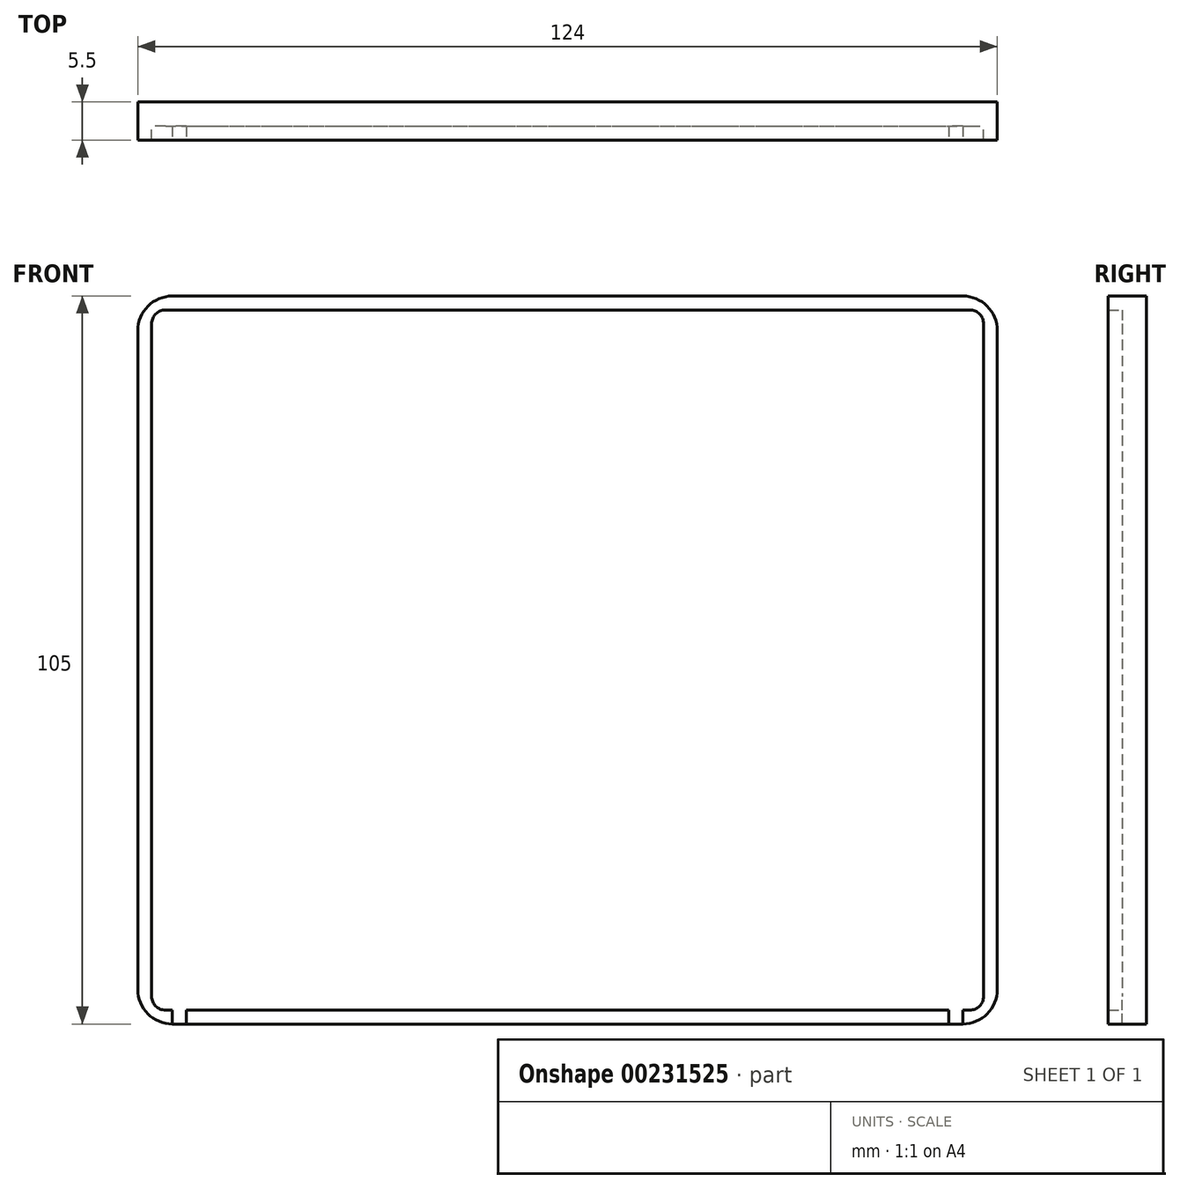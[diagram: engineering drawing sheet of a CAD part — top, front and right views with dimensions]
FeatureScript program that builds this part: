
annotation { "Feature Type Name" : "Feature", "Feature Type Description" : "" }
export const myFeature = defineFeature(function(context is Context, id is Id, definition is map)
    precondition{}
    {
        {
            var Q0;
            Q0=qCreatedBy(makeId("Front.planeOp"),FACE);
            var sketch = newSketch(context, id + "F0", { "sketchPlane" : qUnion([Q0])});
            skLineSegment(sketch, "E0.bottom", {"start": v(62, -52.5) * mm, "end": v(-62, -52.5) * mm});
            skLineSegment(sketch, "E0.top", {"start": v(62, 52.5) * mm, "end": v(-62, 52.5) * mm});
            skLineSegment(sketch, "E0.left", {"start": v(62, -52.5) * mm, "end": v(62, 52.5) * mm});
            skLineSegment(sketch, "E0.right", {"start": v(-62, -52.5) * mm, "end": v(-62, 52.5) * mm});
            skPoint(sketch, "E0.middle", {"position": v(0, 0) * mm});
            skLineSegment(sketch, "E1.bottom", {"start": v(-60, 50.5) * mm, "end": v(60, 50.5) * mm});
            skLineSegment(sketch, "E1.top", {"start": v(-60, -50.5) * mm, "end": v(60, -50.5) * mm});
            skLineSegment(sketch, "E1.left", {"start": v(-60, 50.5) * mm, "end": v(-60, -50.5) * mm});
            skLineSegment(sketch, "E1.right", {"start": v(60, 50.5) * mm, "end": v(60, -50.5) * mm});
            skSolve(sketch);
        }
        {
            var Q0;
            Q0=makeQuery(id+"F0.imprint","IMPRINT",FACE,{"disambiguationData":[TD([[makeQuery(id+"F0.imprint","IMPRINT",EDGE,{"derivedFrom":sQuery(id+"F0.wireOp",EDGE,"E1.bottom")}),-1.0]])]});
            extrude(context, id + "F1", {"entities" : qUnion([Q0]), "depth" : 4 * mm});
        }
        {
            var Q0;
            Q0 = qSketchRegion(id + "F0", true);
            extrude(context, id + "F2", {"entities" : qUnion([Q0]), "operationType" : NewBodyOperationType.ADD, "depth" : 5 * mm});
        }
        {
            var Q0;
            Q0=makeQuery(id+"F2.opExtrude","CAP_FACE",FACE,{"disambiguationData":[OSD([sQuery(id+"F0.wireOp",EDGE,"E0.bottom"),sQuery(id+"F0.wireOp",EDGE,"E0.top"),sQuery(id+"F0.wireOp",EDGE,"E0.left"),sQuery(id+"F0.wireOp",EDGE,"E0.right"),sQuery(id+"F0.wireOp",EDGE,"E1.bottom"),sQuery(id+"F0.wireOp",EDGE,"E1.top"),sQuery(id+"F0.wireOp",EDGE,"E1.left"),sQuery(id+"F0.wireOp",EDGE,"E1.right")])],"isStart":false});
            extrude(context, id + "F3", {"entities" : qUnion([Q0]), "operationType" : NewBodyOperationType.ADD, "depth" : .5 * mm, "offsetDistance" : 25 * mm});
        }
        {
            var Q0;
            {var subQ0=sQuery(id+"F0.wireOp",EDGE,"E0.left");var subQ1=sQuery(id+"F0.wireOp",EDGE,"E0.bottom");Q0=makeQuery(id+"F3.boolean.opBoolean","MERGE",EDGE,{"derivedFrom":[makeQuery(id+"F2.opExtrude","SWEPT_EDGE",EDGE,{"disambiguationData":[OSD([subQ1,subQ0])]}),makeQuery(id+"F3.opExtrude","SWEPT_EDGE",EDGE,{"disambiguationData":[OSD([subQ1,subQ0])]})]});}
            var Q1;
            {var subQ0=sQuery(id+"F0.wireOp",EDGE,"E0.right");var subQ1=sQuery(id+"F0.wireOp",EDGE,"E0.bottom");Q1=makeQuery(id+"F3.boolean.opBoolean","MERGE",EDGE,{"derivedFrom":[makeQuery(id+"F2.opExtrude","SWEPT_EDGE",EDGE,{"disambiguationData":[OSD([subQ1,subQ0])]}),makeQuery(id+"F3.opExtrude","SWEPT_EDGE",EDGE,{"disambiguationData":[OSD([subQ1,subQ0])]})]});}
            var Q2;
            {var subQ0=sQuery(id+"F0.wireOp",EDGE,"E0.right");var subQ1=sQuery(id+"F0.wireOp",EDGE,"E0.top");Q2=makeQuery(id+"F3.boolean.opBoolean","MERGE",EDGE,{"derivedFrom":[makeQuery(id+"F2.opExtrude","SWEPT_EDGE",EDGE,{"disambiguationData":[OSD([subQ1,subQ0])]}),makeQuery(id+"F3.opExtrude","SWEPT_EDGE",EDGE,{"disambiguationData":[OSD([subQ1,subQ0])]})]});}
            var Q3;
            {var subQ0=sQuery(id+"F0.wireOp",EDGE,"E0.left");var subQ1=sQuery(id+"F0.wireOp",EDGE,"E0.top");Q3=makeQuery(id+"F3.boolean.opBoolean","MERGE",EDGE,{"derivedFrom":[makeQuery(id+"F2.opExtrude","SWEPT_EDGE",EDGE,{"disambiguationData":[OSD([subQ1,subQ0])]}),makeQuery(id+"F3.opExtrude","SWEPT_EDGE",EDGE,{"disambiguationData":[OSD([subQ1,subQ0])]})]});}
            fillet(context, id + "F4", {"entities" : qUnion([Q0, Q1, Q2, Q3]), "radius" : 5 * mm, "tangentPropagation" : true, "allowEdgeOverflow" : false});
        }
        {
            var Q0;
            {var subQ0=sQuery(id+"F0.wireOp",EDGE,"E1.right");var subQ1=sQuery(id+"F0.wireOp",EDGE,"E1.bottom");Q0=makeQuery(id+"F3.boolean.opBoolean","MERGE",EDGE,{"derivedFrom":[makeQuery(id+"F2.opExtrude","SWEPT_EDGE",EDGE,{"disambiguationData":[OSD([subQ1,subQ0])]}),makeQuery(id+"F3.opExtrude","SWEPT_EDGE",EDGE,{"disambiguationData":[OSD([subQ1,subQ0])]})]});}
            var Q1;
            {var subQ0=sQuery(id+"F0.wireOp",EDGE,"E1.left");var subQ1=sQuery(id+"F0.wireOp",EDGE,"E1.top");Q1=makeQuery(id+"F3.boolean.opBoolean","MERGE",EDGE,{"derivedFrom":[makeQuery(id+"F2.opExtrude","SWEPT_EDGE",EDGE,{"disambiguationData":[OSD([subQ1,subQ0])]}),makeQuery(id+"F3.opExtrude","SWEPT_EDGE",EDGE,{"disambiguationData":[OSD([subQ1,subQ0])]})]});}
            var Q2;
            {var subQ0=sQuery(id+"F0.wireOp",EDGE,"E1.right");var subQ1=sQuery(id+"F0.wireOp",EDGE,"E1.top");Q2=makeQuery(id+"F3.boolean.opBoolean","MERGE",EDGE,{"derivedFrom":[makeQuery(id+"F2.opExtrude","SWEPT_EDGE",EDGE,{"disambiguationData":[OSD([subQ1,subQ0])]}),makeQuery(id+"F3.opExtrude","SWEPT_EDGE",EDGE,{"disambiguationData":[OSD([subQ1,subQ0])]})]});}
            var Q3;
            {var subQ0=sQuery(id+"F0.wireOp",EDGE,"E1.left");var subQ1=sQuery(id+"F0.wireOp",EDGE,"E1.bottom");Q3=makeQuery(id+"F3.boolean.opBoolean","MERGE",EDGE,{"derivedFrom":[makeQuery(id+"F2.opExtrude","SWEPT_EDGE",EDGE,{"disambiguationData":[OSD([subQ1,subQ0])]}),makeQuery(id+"F3.opExtrude","SWEPT_EDGE",EDGE,{"disambiguationData":[OSD([subQ1,subQ0])]})]});}
            fillet(context, id + "F5", {"entities" : qUnion([Q0, Q1, Q2, Q3]), "radius" : 2 * mm, "tangentPropagation" : true, "allowEdgeOverflow" : false});
        }
        {
            var Q0;
            Q0=makeQuery(id+"F3.opExtrude","CAP_FACE",FACE,{"disambiguationData":[OSD([sQuery(id+"F0.wireOp",EDGE,"E0.bottom"),sQuery(id+"F0.wireOp",EDGE,"E0.top"),sQuery(id+"F0.wireOp",EDGE,"E0.left"),sQuery(id+"F0.wireOp",EDGE,"E0.right"),sQuery(id+"F0.wireOp",EDGE,"E1.bottom"),sQuery(id+"F0.wireOp",EDGE,"E1.top"),sQuery(id+"F0.wireOp",EDGE,"E1.left"),sQuery(id+"F0.wireOp",EDGE,"E1.right")])],"isStart":false});
            var sketch = newSketch(context, id + "F6", { "sketchPlane" : qUnion([Q0])});
            skLineSegment(sketch, "E2", {"start": v(-57, -52.5) * mm, "end": v(-57, -50.5) * mm});
            skLineSegment(sketch, "E3", {"start": v(-55, -50.5) * mm, "end": v(-55, -52.5) * mm});
            skLineSegment(sketch, "E4", {"start": v(-55, -52.5) * mm, "end": v(-57, -52.5) * mm});
            skLineSegment(sketch, "E5", {"start": v(-57, -50.5) * mm, "end": v(-55, -50.5) * mm});
            skSolve(sketch);
        }
        {
            var Q0;
            Q0=makeQuery(id+"F6.imprint","IMPRINT",FACE,{"disambiguationData":[TD([[makeQuery(id+"F6.imprint","IMPRINT",EDGE,{"derivedFrom":sQuery(id+"F6.wireOp",EDGE,"E2")}),-1.0]])]});
            extrude(context, id + "F7", {"entities" : qUnion([Q0]), "operationType" : NewBodyOperationType.REMOVE, "oppositeDirection" : true, "depth" : 1.5 * mm, "offsetDistance" : 25 * mm});
        }
        {
            var Q0;
            Q0=makeQuery(id+"F3.opExtrude","CAP_FACE",FACE,{"disambiguationData":[OSD([sQuery(id+"F0.wireOp",EDGE,"E0.bottom"),sQuery(id+"F0.wireOp",EDGE,"E0.top"),sQuery(id+"F0.wireOp",EDGE,"E0.left"),sQuery(id+"F0.wireOp",EDGE,"E0.right"),sQuery(id+"F0.wireOp",EDGE,"E1.bottom"),sQuery(id+"F0.wireOp",EDGE,"E1.top"),sQuery(id+"F0.wireOp",EDGE,"E1.left"),sQuery(id+"F0.wireOp",EDGE,"E1.right")])],"isStart":false});
            var sketch = newSketch(context, id + "F8", { "sketchPlane" : qUnion([Q0])});
            skLineSegment(sketch, "E6", {"start": v(57, -52.5) * mm, "end": v(57, -50.5) * mm});
            skLineSegment(sketch, "E7", {"start": v(57, -50.5) * mm, "end": v(55, -50.5) * mm});
            skLineSegment(sketch, "E8", {"start": v(55, -50.5) * mm, "end": v(55, -52.5) * mm});
            skLineSegment(sketch, "E9", {"start": v(55, -52.5) * mm, "end": v(57, -52.5) * mm});
            skSolve(sketch);
        }
        {
            var Q0;
            Q0=makeQuery(id+"F8.imprint","IMPRINT",FACE,{"disambiguationData":[TD([[makeQuery(id+"F8.imprint","IMPRINT",EDGE,{"derivedFrom":sQuery(id+"F8.wireOp",EDGE,"E6")}),1.0]])]});
            extrude(context, id + "F9", {"entities" : qUnion([Q0]), "operationType" : NewBodyOperationType.REMOVE, "oppositeDirection" : true, "depth" : 1.5 * mm, "offsetDistance" : 25 * mm});
        }
        {
            var Q0;
            Q0=makeQuery(id+"F9.boolean.opBoolean","MERGE",FACE,{"derivedFrom":[makeQuery(id+"F7.boolean.opBoolean","MERGE",FACE,{"derivedFrom":[makeQuery(id+"F1.opExtrude","CAP_FACE",FACE,{"disambiguationData":[OSD([sQuery(id+"F0.wireOp",EDGE,"E1.bottom"),sQuery(id+"F0.wireOp",EDGE,"E1.top"),sQuery(id+"F0.wireOp",EDGE,"E1.left"),sQuery(id+"F0.wireOp",EDGE,"E1.right")])],"isStart":false}),makeQuery(id+"F7.opExtrude","CAP_FACE",FACE,{"disambiguationData":[OSD([sQuery(id+"F6.wireOp",EDGE,"E2"),sQuery(id+"F6.wireOp",EDGE,"E3"),sQuery(id+"F6.wireOp",EDGE,"E4"),sQuery(id+"F6.wireOp",EDGE,"E5")])],"isStart":false})]}),makeQuery(id+"F9.opExtrude","CAP_FACE",FACE,{"disambiguationData":[OSD([sQuery(id+"F8.wireOp",EDGE,"E6"),sQuery(id+"F8.wireOp",EDGE,"E7"),sQuery(id+"F8.wireOp",EDGE,"E8"),sQuery(id+"F8.wireOp",EDGE,"E9")])],"isStart":false})]});
            extrude(context, id + "F10", {"entities" : qUnion([Q0]), "operationType" : NewBodyOperationType.REMOVE, "oppositeDirection" : true, "depth" : .5 * mm, "offsetDistance" : 25 * mm});
        }
    });
